FCSTD DOCUMENT  (FreeCAD 0.20R29177 +426 (Git))
Label: FallAnim
License: All rights reserved
LicenseURL: http://en.wikipedia.org/wiki/All_rights_reserved
objects: PartDesign::CoordinateSystem×2, Sketcher::SketchObject×1, PartDesign::Body×1
note: 4 computed .brp shape members not serialized (recipe doc carries the construction recipe); baked Part::Feature solids carry a one-line shape summary decoded from their .brp
EXTERNAL_REF file=assembly4.FCStd obj=Variables

FEATURE [PartDesign::CoordinateSystem] LCS_Origin
  AttacherType = Attacher::AttachEngine3D
  MapMode = 2
  Support = -> [X_Axis]
FEATURE [Sketcher::SketchObject] Sketch
  FullyConstrained = true
  MapMode = 5
  Placement = pos=(0,0,0) rot=(1,0,0;1.5708rad)
  Support = -> [XZ_Plane]
  expr: Constraints[2] = assembly4#Variables.FallHandlerVar
  sketch-geometry (1):
    g0: LineSegment StartX=0 StartY=0 StartZ=0 EndX=0 EndY=-900 EndZ=0
  constraints (3):
    c: Coincident(g0,g-1)
    c: PointOnObject(g0,g-2)
    c: DistanceY(g0,g0) = 900
FEATURE [PartDesign::CoordinateSystem] LCS_fallhandler
  AttacherType = Attacher::AttachEngine3D
  MapMode = 7
  Placement = pos=(0,1.998e-13,-900) rot=(0,0,1;0rad)
  Support = -> [Sketch]
FEATURE [PartDesign::Body] fallSketchBody
  Group = -> [LCS_Origin,Sketch,LCS_fallhandler]
  Origin = -> Origin
